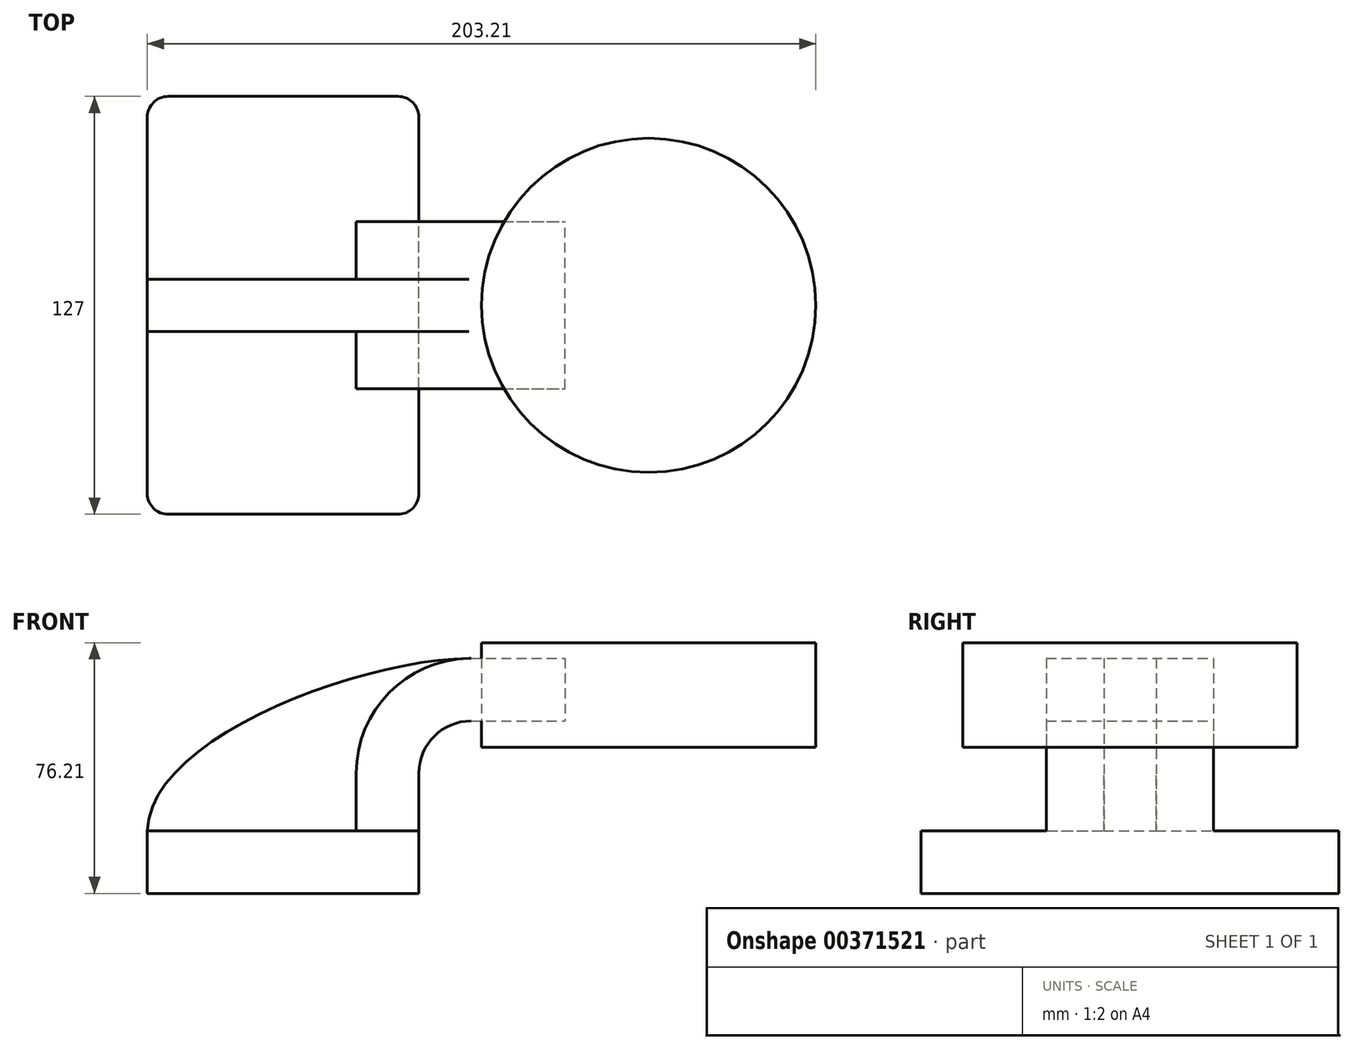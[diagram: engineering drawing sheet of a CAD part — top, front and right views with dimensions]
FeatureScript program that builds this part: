
annotation { "Feature Type Name" : "Feature", "Feature Type Description" : "" }
export const myFeature = defineFeature(function(context is Context, id is Id, definition is map)
    precondition{}
    {
        {
            var Q0;
            Q0=qCreatedBy(makeId("Front.planeOp"),FACE);
            var sketch = newSketch(context, id + "F0", { "sketchPlane" : qUnion([Q0])});
            skLineSegment(sketch, "E0.bottom", {"start": v(41.27, 9.53) * mm, "end": v(-41.28, 9.53) * mm});
            skLineSegment(sketch, "E0.top", {"start": v(41.28, -9.52) * mm, "end": v(-41.27, -9.52) * mm});
            skLineSegment(sketch, "E0.left", {"start": v(41.28, 9.53) * mm, "end": v(41.28, -9.52) * mm});
            skLineSegment(sketch, "E0.right", {"start": v(-41.28, 9.53) * mm, "end": v(-41.27, -9.52) * mm});
            skPoint(sketch, "E0.middle", {"position": v(0, 0) * mm});
            skLineSegment(sketch, "E1.bottom", {"start": v(111.12, 34.93) * mm, "end": v(60.32, 34.93) * mm});
            skLineSegment(sketch, "E1.top", {"start": v(111.12, 66.68) * mm, "end": v(60.33, 66.68) * mm});
            skLineSegment(sketch, "E1.left", {"start": v(111.12, 34.93) * mm, "end": v(111.12, 66.68) * mm});
            skLineSegment(sketch, "E1.right", {"start": v(60.33, 34.93) * mm, "end": v(60.33, 66.68) * mm});
            skPoint(sketch, "E1.middle", {"position": v(85.72, 50.8) * mm});
            skLineSegment(sketch, "E2", {"start": v(41.27, 9.53) * mm, "end": v(41.27, 27) * mm});
            skArc(sketch, "E3", {"start": v(41.28, 27) * mm, "mid": v(45.92, 38.23) * mm, "end": v(57.15, 42.88) * mm});
            skLineSegment(sketch, "E4", {"start": v(57.15, 42.88) * mm, "end": v(85.72, 42.88) * mm});
            skLineSegment(sketch, "E5.0", {"start": v(57.15, 61.93) * mm, "end": v(85.73, 61.93) * mm});
            skArc(sketch, "E5.1", {"start": v(22.23, 27) * mm, "mid": v(32.45, 51.7) * mm, "end": v(57.15, 61.93) * mm});
            skLineSegment(sketch, "E5.2", {"start": v(22.22, 9.53) * mm, "end": v(22.22, 27) * mm});
            skLineSegment(sketch, "E6", {"start": v(85.73, 61.93) * mm, "end": v(85.73, 42.88) * mm});
            skFitSpline(sketch, "E7", {"points": [v(57.15, 61.93) * mm, v(-41.28, 9.52) * mm], "startDerivative": vector(-99.73, -0.5) * mm, "endDerivative": vector(-2.35, -85.76) * mm});
            skSolve(sketch);
        }
        {
            var Q0;
            Q0=makeQuery(id+"F0.imprint","IMPRINT",FACE,{"disambiguationData":[TD([[makeQuery(id+"F0.imprint","IMPRINT",EDGE,{"derivedFrom":sQuery(id+"F0.wireOp",EDGE,"E0.top")}),-1.0]])]});
            extrude(context, id + "F1", {"entities" : qUnion([Q0]), "endBound" : BoundingType.SYMMETRIC, "depth" : 127 * mm});
        }
        {
            var Q0;
            {var subQ1=sQuery(id+"F0.wireOp",EDGE,"E2");Q0=makeQuery(id+"F0.imprint","IMPRINT",FACE,{"disambiguationData":[TD([[makeQuery(id+"F0.imprint","IMPRINT",EDGE,{"derivedFrom":subQ1}),1.0]])]});}
            var Q1;
            {var subQ5=sQuery(id+"F0.wireOp",EDGE,"E6");Q1=makeQuery(id+"F0.imprint","IMPRINT",FACE,{"disambiguationData":[TD([[makeQuery(id+"F0.imprint","IMPRINT",EDGE,{"derivedFrom":subQ5}),-1.0]])]});}
            extrude(context, id + "F2", {"entities" : qUnion([Q0, Q1]), "operationType" : NewBodyOperationType.ADD, "endBound" : BoundingType.SYMMETRIC, "depth" : 50.8 * mm});
        }
        {
            var Q0;
            {var subQ3=sQuery(id+"F0.wireOp",EDGE,"E5.2");Q0=makeQuery(id+"F0.imprint","IMPRINT",FACE,{"disambiguationData":[TD([[makeQuery(id+"F0.imprint","IMPRINT",EDGE,{"derivedFrom":subQ3}),1.0]])]});}
            extrude(context, id + "F3", {"entities" : qUnion([Q0]), "operationType" : NewBodyOperationType.ADD, "endBound" : BoundingType.SYMMETRIC, "depth" : 15.88 * mm});
        }
        {
            var Q0;
            {var subQ1=sQuery(id+"F0.wireOp",EDGE,"E1.bottom");Q0=makeQuery(id+"F0.imprint","IMPRINT",FACE,{"disambiguationData":[TD([[makeQuery(id+"F0.imprint","IMPRINT",EDGE,{"derivedFrom":subQ1}),-1.0]])]});}
            var Q1;
            {var subQ5=sQuery(id+"F0.wireOp",EDGE,"E6");Q1=makeQuery(id+"F0.imprint","IMPRINT",FACE,{"disambiguationData":[TD([[makeQuery(id+"F0.imprint","IMPRINT",EDGE,{"derivedFrom":subQ5}),-1.0]])]});}
            var Q2;
            Q2=sQuery(id+"F0.wireOp",EDGE,"E1.left");
            revolve(context, id + "F4", {"entities" : qUnion([Q0, Q1]), "axis" : qUnion([Q2]), "revolveType" : RevolveType.FULL});
        }
        {
            var Q0;
            Q0=makeQuery(id+"F1.opExtrude","CAP_EDGE",EDGE,{"disambiguationData":[OSD([sQuery(id+"F0.wireOp",EDGE,"E0.left")])],"isStart":false});
            var Q1;
            Q1=makeQuery(id+"F1.opExtrude","CAP_EDGE",EDGE,{"disambiguationData":[OSD([sQuery(id+"F0.wireOp",EDGE,"E0.right")])],"isStart":false});
            var Q2;
            Q2=makeQuery(id+"F1.opExtrude","CAP_EDGE",EDGE,{"disambiguationData":[OSD([sQuery(id+"F0.wireOp",EDGE,"E0.right")])],"isStart":true});
            var Q3;
            Q3=makeQuery(id+"F1.opExtrude","CAP_EDGE",EDGE,{"disambiguationData":[OSD([sQuery(id+"F0.wireOp",EDGE,"E0.left")])],"isStart":true});
            fillet(context, id + "F5", {"entities" : qUnion([Q0, Q1, Q2, Q3]), "radius" : 6.35 * mm, "tangentPropagation" : true, "allowEdgeOverflow" : false});
        }
    });
